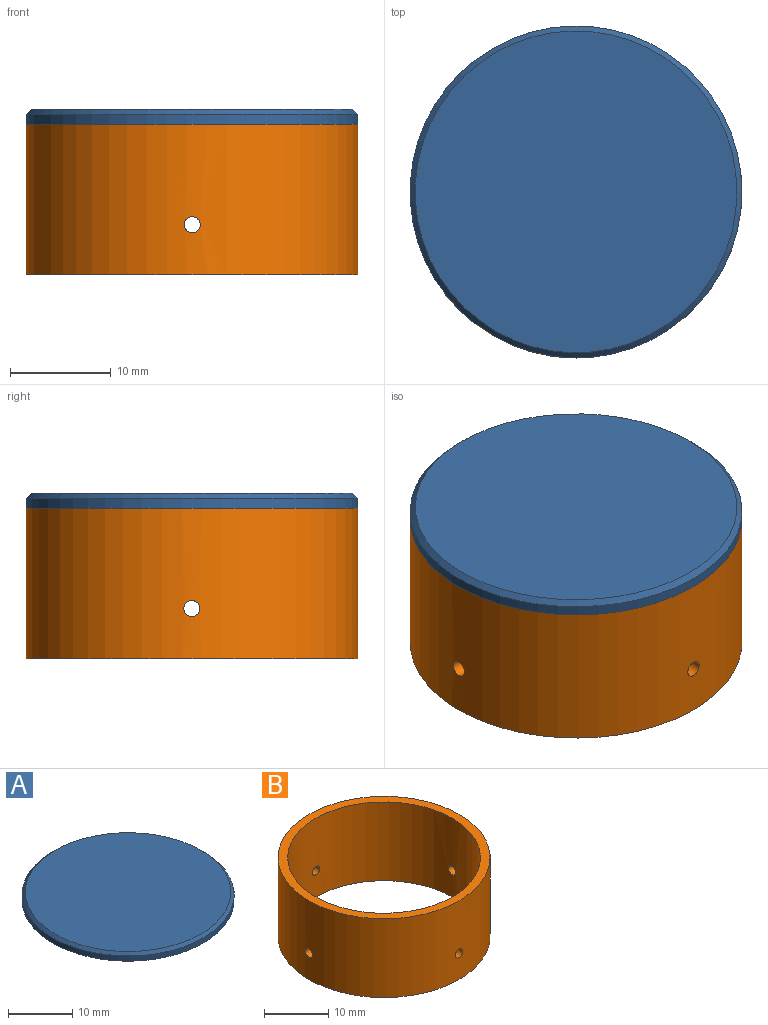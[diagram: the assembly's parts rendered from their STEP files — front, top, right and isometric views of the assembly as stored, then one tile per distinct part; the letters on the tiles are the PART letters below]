
ASSEMBLY  parts=2 mates=1
PART A: 4 faces, bbox 33x33x1.5 mm
  f0: cylinder r=16.5mm len=33mm, axis (0,0,-1), area 103.7mm2, adj f2,f3
  f1: plane 32x32mm, normal (0,0,1), area 804.2mm2, adj f3
  f2: plane 33x33mm, normal (0,0,-1), area 855.3mm2, adj f0
  f3: cone r=16mm half-angle=45deg, axis (0,0,-1), area 72.2mm2, adj f0,f1
PART B: 8 faces, bbox 33x33x15 mm
  f0: cylinder r=15mm len=30mm, axis (0,0,-1), area 1405.7mm2, adj f2,f3,f4,f5,f6,f7
  f1: cylinder r=16.5mm len=33mm, axis (0,0,-1), area 1547.1mm2, adj f2,f3,f4,f5,f6,f7
  f2: plane 33x33mm, normal (0,0,1), area 148.4mm2, adj f0,f1
  f3: plane 33x33mm, normal (0,0,-1), area 148.4mm2, adj f0,f1
  f4: cylinder r=0.8mm len=1.6mm, axis (1,0,0), area 7.5mm2, adj f0,f1
  f5: cylinder r=0.8mm len=1.6mm, axis (1,0,0), area 7.5mm2, adj f0,f1
  f6: cylinder r=0.8mm len=1.6mm, axis (0,-1,0), area 7.5mm2, adj f0,f1
  f7: cylinder r=0.8mm len=1.6mm, axis (0,-1,0), area 7.5mm2, adj f0,f1
PLACE A rot(axis=(0,1,0),0deg) t=(-54.87,110.63,-26.44)mm
PLACE B rot(axis=(0,1,0),0deg) t=(-54.87,110.63,-41.44)mm
MATE fastened B.f1 <-> A.f0  axis (0,0,1) through (-54.87,110.63,-26.44)mm
